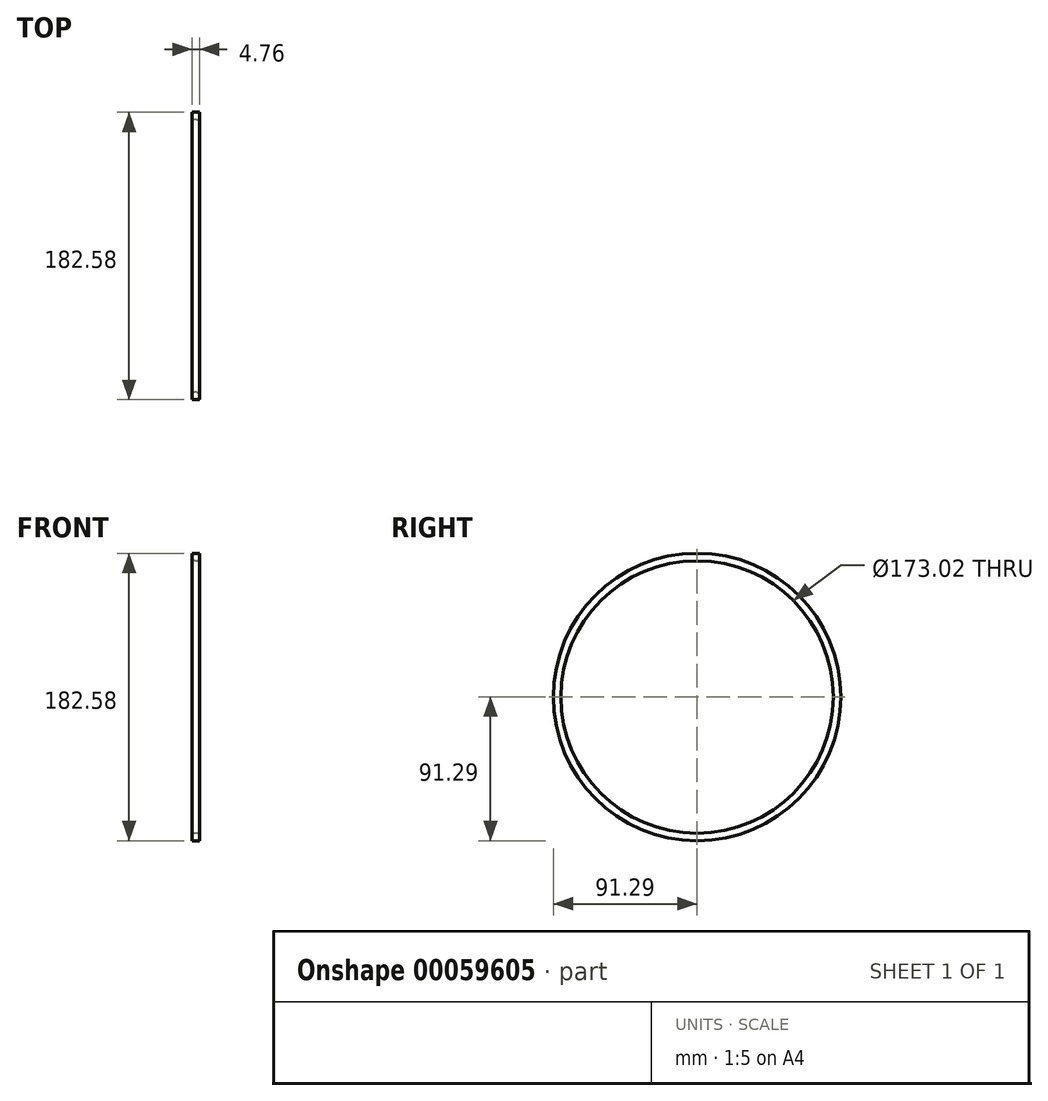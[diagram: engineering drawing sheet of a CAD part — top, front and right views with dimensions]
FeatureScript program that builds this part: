
annotation { "Feature Type Name" : "Feature", "Feature Type Description" : "" }
export const myFeature = defineFeature(function(context is Context, id is Id, definition is map)
    precondition{}
    {
        {
            var Q0;
            Q0=qCreatedBy(makeId("Front.planeOp"),FACE);
            var sketch = newSketch(context, id + "F0", { "sketchPlane" : qUnion([Q0])});
            skLineSegment(sketch, "E0", {"start": v(0, -4.21) * mm, "end": v(0, 0) * mm, "construction": true});
            skLineSegment(sketch, "E1", {"start": v(-19.05, 0) * mm, "end": v(19.38, 0) * mm});
            skLineSegment(sketch, "E2", {"start": v(0, 0) * mm, "end": v(0, 88.9) * mm, "construction": true});
            skLineSegment(sketch, "E3.rect.bottom", {"start": v(2.38, 91.29) * mm, "end": v(-2.38, 91.29) * mm});
            skLineSegment(sketch, "E3.rect.top", {"start": v(2.38, 86.51) * mm, "end": v(-2.38, 86.51) * mm});
            skLineSegment(sketch, "E3.rect.left", {"start": v(2.38, 91.29) * mm, "end": v(2.38, 86.51) * mm});
            skLineSegment(sketch, "E3.rect.right", {"start": v(-2.38, 91.29) * mm, "end": v(-2.38, 86.51) * mm});
            skPoint(sketch, "E3.rect.middle", {"position": v(0, 88.9) * mm});
            skSolve(sketch);
        }
        {
            var Q0;
            Q0 = qSketchRegion(id + "F0", true);
            var Q1;
            Q1=sQuery(id+"F0.wireOp",EDGE,"E1");
            revolve(context, id + "F1", {"entities" : qUnion([Q0]), "axis" : qUnion([Q1]), "revolveType" : RevolveType.FULL});
        }
        {
            var Q0;
            Q0=makeQuery(id+"F1.opRevolve","SWEPT_EDGE",EDGE,{"disambiguationData":[OSD([sQuery(id+"F0.wireOp",EDGE,"E3.rect.top"),sQuery(id+"F0.wireOp",EDGE,"E3.rect.left")])]});
            var Q1;
            Q1=makeQuery(id+"F1.opRevolve","SWEPT_EDGE",EDGE,{"disambiguationData":[OSD([sQuery(id+"F0.wireOp",EDGE,"E3.rect.top"),sQuery(id+"F0.wireOp",EDGE,"E3.rect.right")])]});
            fillet(context, id + "F2", {"entities" : qUnion([Q0, Q1]), "radius" : 1.9 * mm, "tangentPropagation" : true, "allowEdgeOverflow" : false});
        }
    });
